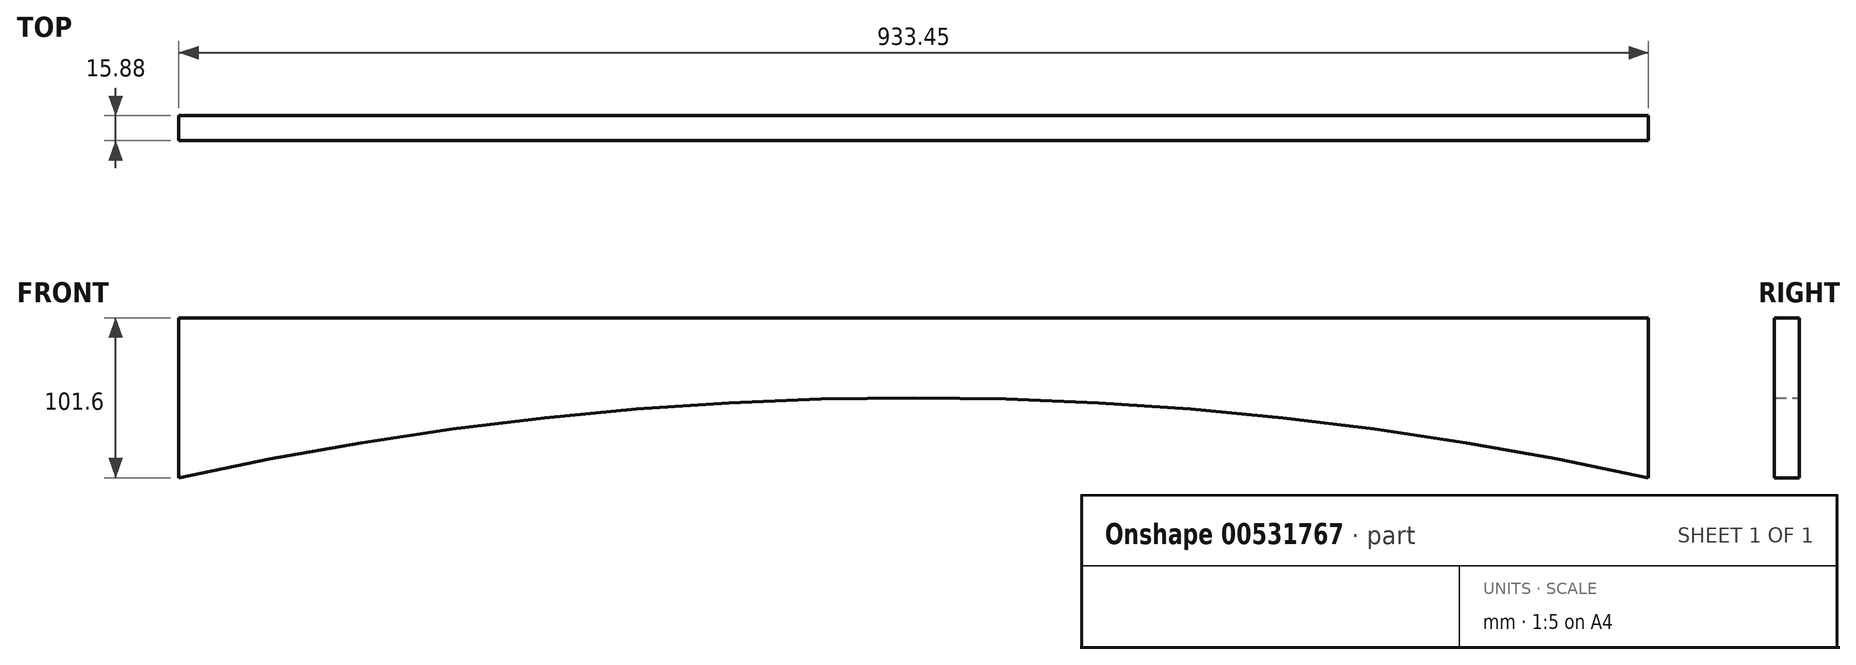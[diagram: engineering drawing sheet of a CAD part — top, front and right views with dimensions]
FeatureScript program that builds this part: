
annotation { "Feature Type Name" : "Feature", "Feature Type Description" : "" }
export const myFeature = defineFeature(function(context is Context, id is Id, definition is map)
    precondition{}
    {
        {
            var Q0;
            Q0=qCreatedBy(makeId("Front.planeOp"),FACE);
            var sketch = newSketch(context, id + "F0", { "sketchPlane" : qUnion([Q0])});
            skLineSegment(sketch, "E0", {"start": v(-70.95, 9.38) * mm, "end": v(862.5, 9.38) * mm});
            skLineSegment(sketch, "E1", {"start": v(862.5, 9.38) * mm, "end": v(862.5, -66.82) * mm});
            skLineSegment(sketch, "E2", {"start": v(-70.95, 9.38) * mm, "end": v(-70.95, -66.82) * mm});
            skArc(sketch, "E3", {"start": v(862.5, -66.82) * mm, "mid": v(395.78, -16.02) * mm, "end": v(-70.95, -66.82) * mm});
            skPoint(sketch, "E4.start.orphan", {"position": v(395.78, 9.38) * mm});
            skSolve(sketch);
        }
        {
            var Q0;
            Q0 = qSketchRegion(id + "F0", true);
            extrude(context, id + "F1", {"entities" : qUnion([Q0]), "depth" : 25.4 * mm, "offsetDistance" : 25.4 * mm});
        }
        {
            var Q0;
            Q0=makeQuery(id+"F1.opExtrude","SWEPT_BODY",BODY,{"disambiguationData":[OSD([sQuery(id+"F0.wireOp",EDGE,"E0"),sQuery(id+"F0.wireOp",EDGE,"E1"),sQuery(id+"F0.wireOp",EDGE,"E2"),sQuery(id+"F0.wireOp",EDGE,"E3")])]});
            deleteBodies(context, id + "F2", {"entities" : qUnion([Q0])});
        }
        {
            var Q0;
            Q0=qCreatedBy(makeId("Front.planeOp"),FACE);
            var sketch = newSketch(context, id + "F3", { "sketchPlane" : qUnion([Q0])});
            skLineSegment(sketch, "E5", {"start": v(-74.68, 10.84) * mm, "end": v(858.77, 10.84) * mm});
            skLineSegment(sketch, "E6", {"start": v(858.77, 10.84) * mm, "end": v(858.77, -90.76) * mm});
            skLineSegment(sketch, "E7", {"start": v(-74.68, 10.84) * mm, "end": v(-74.68, -90.76) * mm});
            skArc(sketch, "E8", {"start": v(858.77, -90.76) * mm, "mid": v(392.05, -39.96) * mm, "end": v(-74.68, -90.76) * mm});
            skPoint(sketch, "E9.start.orphan", {"position": v(392.05, 10.84) * mm});
            skSolve(sketch);
        }
        {
            var Q0;
            Q0 = qSketchRegion(id + "F3", true);
            extrude(context, id + "F4", {"entities" : qUnion([Q0]), "depth" : 15.88 * mm, "offsetDistance" : 25.4 * mm});
        }
    });
